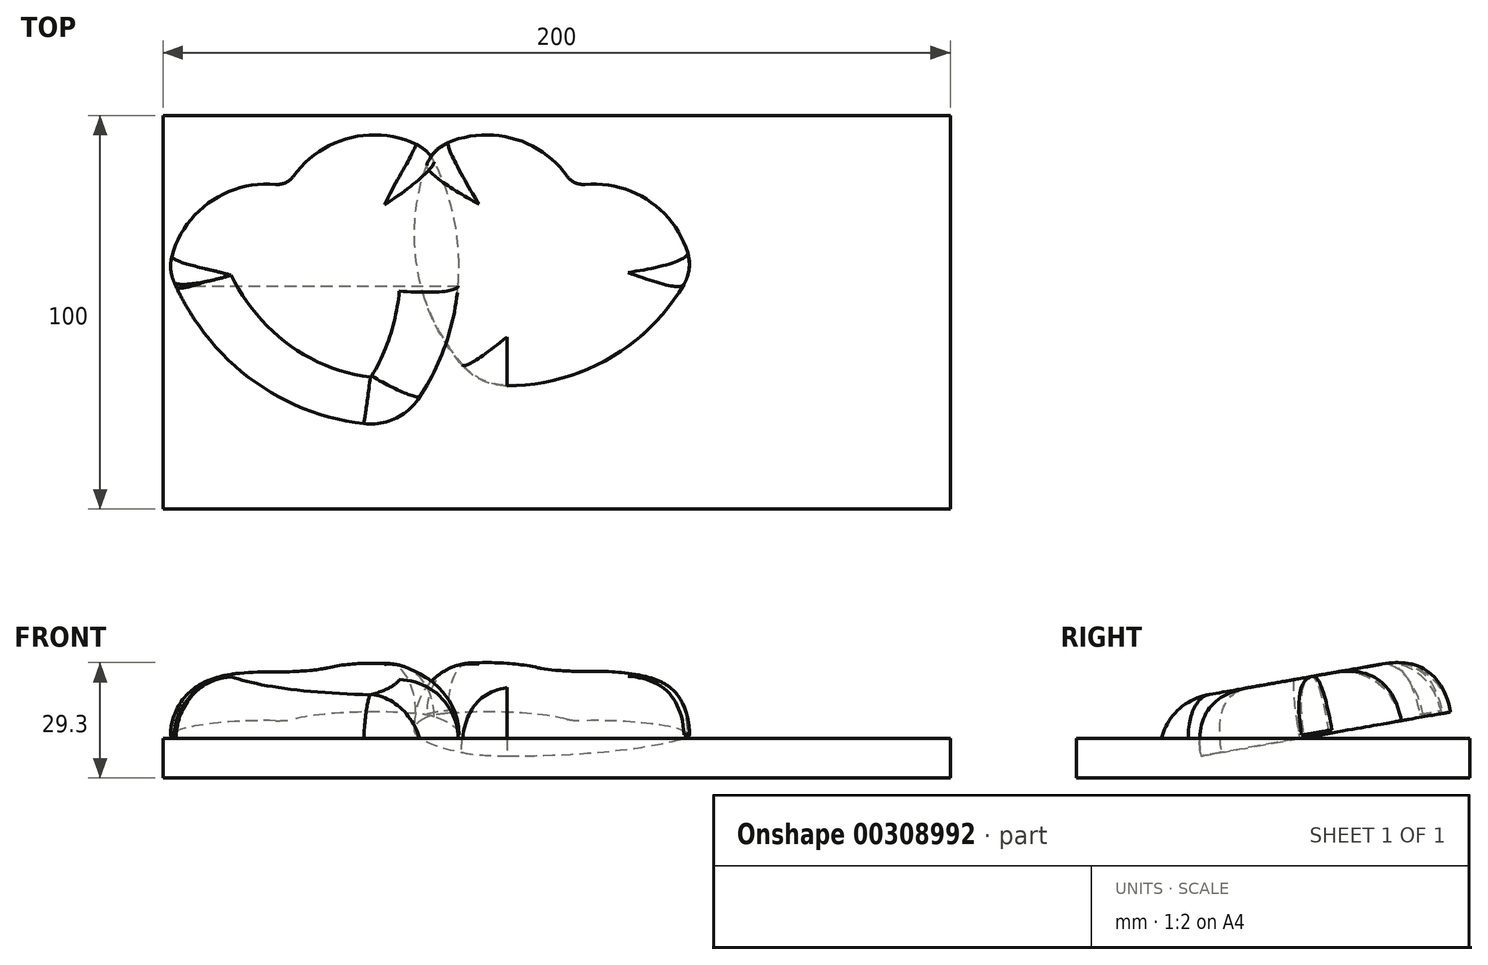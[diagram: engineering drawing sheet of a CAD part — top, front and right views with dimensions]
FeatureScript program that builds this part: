
annotation { "Feature Type Name" : "Feature", "Feature Type Description" : "" }
export const myFeature = defineFeature(function(context is Context, id is Id, definition is map)
    precondition{}
    {
        {
            var Q0;
            Q0=qCreatedBy(makeId("Top.planeOp"),FACE);
            var sketch = newSketch(context, id + "F0", { "sketchPlane" : qUnion([Q0])});
            skLineSegment(sketch, "E0.bottom", {"start": v(0, 0) * mm, "end": v(200, 0) * mm});
            skLineSegment(sketch, "E0.top", {"start": v(0, 100) * mm, "end": v(200, 100) * mm});
            skLineSegment(sketch, "E0.left", {"start": v(0, 0) * mm, "end": v(0, 100) * mm});
            skLineSegment(sketch, "E0.right", {"start": v(200, 0) * mm, "end": v(200, 100) * mm});
            skSolve(sketch);
        }
        {
            var Q0;
            Q0=makeQuery(id+"F0.imprint","IMPRINT",FACE,{"disambiguationData":[TD([[makeQuery(id+"F0.imprint","IMPRINT",EDGE,{"derivedFrom":sQuery(id+"F0.wireOp",EDGE,"E0.bottom")}),1.0]])]});
            extrude(context, id + "F1", {"entities" : qUnion([Q0]), "depth" : 10 * mm});
        }
        {
            var Q0;
            Q0=qCreatedBy(makeId("Top.planeOp"),FACE);
            cPlane(context, id + "F2", {"entities" : qUnion([Q0]), "cplaneType" : CPlaneType.OFFSET, "offset" : 10 * mm, "width" : 150 * mm, "height" : 150 * mm});
        }
        {
            var Q0;
            Q0=qCreatedBy(id+"F2.planeOp",FACE);
            var Q1;
            Q1=makeQuery(id+"F1.opExtrude","CAP_EDGE",EDGE,{"disambiguationData":[OSD([sQuery(id+"F0.wireOp",EDGE,"E0.bottom")])],"isStart":true});
            cPlane(context, id + "F3", {"entities" : qUnion([Q0, Q1]), "cplaneType" : CPlaneType.LINE_ANGLE, "offset" : 25 * mm, "angle" : 170 * degree, "oppositeDirection" : true, "width" : 150 * mm, "height" : 150 * mm});
        }
        {
            var Q0;
            Q0=qCreatedBy(id+"F3.planeOp",FACE);
            var sketch = newSketch(context, id + "F4", { "sketchPlane" : qUnion([Q0])});
            skArc(sketch, "E1", {"start": v(28.58, 83.78) * mm, "mid": v(12.06, 79.35) * mm, "end": v(2.25, 65.33) * mm});
            skArc(sketch, "E2", {"start": v(64.18, 94.2) * mm, "mid": v(47.14, 95.7) * mm, "end": v(33.12, 85.9) * mm});
            skArc(sketch, "E3", {"start": v(65.18, 29.74) * mm, "mid": v(75.06, 59.17) * mm, "end": v(68.9, 89.6) * mm});
            skArc(sketch, "E4", {"start": v(2.75, 58.75) * mm, "mid": v(22.1, 34.48) * mm, "end": v(51, 23.12) * mm});
            skArc(sketch, "E5", {"start": v(102.66, 85.9) * mm, "mid": v(89.03, 95.6) * mm, "end": v(72.33, 94.54) * mm});
            skArc(sketch, "E6", {"start": v(133.3, 66.1) * mm, "mid": v(123.38, 79.58) * mm, "end": v(107.19, 83.78) * mm});
            skArc(sketch, "E7", {"start": v(66.88, 88.77) * mm, "mid": v(64.5, 61.95) * mm, "end": v(75.79, 37.5) * mm});
            skArc(sketch, "E8", {"start": v(87.39, 32.1) * mm, "mid": v(113.38, 39.15) * mm, "end": v(132.4, 58.22) * mm});
            skLineSegment(sketch, "E9", {"start": v(26.4, 58.88) * mm, "end": v(53.6, 71.56) * mm, "construction": true});
            skLineSegment(sketch, "E10", {"start": v(31.55, 83.34) * mm, "end": v(40, 65.22) * mm, "construction": true});
            skLineSegment(sketch, "E11", {"start": v(82.18, 71.56) * mm, "end": v(109.37, 58.88) * mm, "construction": true});
            skLineSegment(sketch, "E12", {"start": v(104.23, 83.34) * mm, "end": v(95.77, 65.22) * mm, "construction": true});
            skPoint(sketch, "E13.visualSharp", {"position": v(1.56, 61.67) * mm});
            skArc(sketch, "E13.filletArc", {"start": v(2.25, 65.33) * mm, "mid": v(1.94, 62) * mm, "end": v(2.75, 58.75) * mm});
            skPoint(sketch, "E14.visualSharp", {"position": v(67.42, 92.38) * mm});
            skArc(sketch, "E14.filletArc", {"start": v(68.9, 89.6) * mm, "mid": v(66.93, 92.3) * mm, "end": v(64.18, 94.2) * mm});
            skPoint(sketch, "E15.visualSharp", {"position": v(68.35, 92.38) * mm});
            skArc(sketch, "E15.filletArc", {"start": v(72.33, 94.54) * mm, "mid": v(69, 92.22) * mm, "end": v(66.88, 88.77) * mm});
            skPoint(sketch, "E16.visualSharp", {"position": v(134.21, 61.67) * mm});
            skArc(sketch, "E16.filletArc", {"start": v(132.4, 58.22) * mm, "mid": v(133.66, 62.07) * mm, "end": v(133.3, 66.1) * mm});
            skPoint(sketch, "E17.visualSharp", {"position": v(104.23, 83.34) * mm});
            skArc(sketch, "E17.filletArc", {"start": v(102.66, 85.9) * mm, "mid": v(104.64, 84.23) * mm, "end": v(107.19, 83.78) * mm});
            skPoint(sketch, "E18.visualSharp", {"position": v(31.55, 83.34) * mm});
            skArc(sketch, "E18.filletArc", {"start": v(28.58, 83.78) * mm, "mid": v(31.13, 84.23) * mm, "end": v(33.12, 85.9) * mm});
            skPoint(sketch, "E19.visualSharp", {"position": v(59.79, 22.78) * mm});
            skArc(sketch, "E19.filletArc", {"start": v(51, 23.12) * mm, "mid": v(59.02, 24.43) * mm, "end": v(65.18, 29.74) * mm});
            skPoint(sketch, "E20.visualSharp", {"position": v(80.52, 32.51) * mm});
            skArc(sketch, "E20.filletArc", {"start": v(75.79, 37.5) * mm, "mid": v(80.98, 33.5) * mm, "end": v(87.39, 32.1) * mm});
            skLineSegment(sketch, "E21", {"start": v(11.91, 62.75) * mm, "end": v(35.93, 73.95) * mm, "construction": true});
            skLineSegment(sketch, "E22", {"start": v(59.95, 85.15) * mm, "end": v(35.93, 73.95) * mm, "construction": true});
            skLineSegment(sketch, "E23", {"start": v(76.27, 85.34) * mm, "end": v(100, 74.28) * mm, "construction": true});
            skPoint(sketch, "E23.endSnap0", {"position": v(100, 74.28) * mm});
            skLineSegment(sketch, "E24", {"start": v(100, 74.28) * mm, "end": v(123.73, 63.22) * mm, "construction": true});
            skSolve(sketch);
        }
        {
            var Q0;
            Q0=makeQuery(id+"F4.imprint","IMPRINT",FACE,{"disambiguationData":[TD([[makeQuery(id+"F4.imprint","IMPRINT",EDGE,{"derivedFrom":sQuery(id+"F4.wireOp",EDGE,"E1")}),1.0]])]});
            var Q1;
            {var subQ0=sQuery(id+"F4.wireOp",EDGE,"E14.filletArc");var subQ1=sQuery(id+"F4.wireOp",EDGE,"E3");var subQ2=makeQuery(id+"F4.imprint","INTERSECT",VERTEX,{"derivedFrom":[subQ1,subQ0]});Q1=makeQuery(id+"F4.imprint","IMPRINT",FACE,{"disambiguationData":[TD([[makeQuery(id+"F4.imprint","IMPRINT",EDGE,{"disambiguationData":[TD([[subQ2,1.0]])],"derivedFrom":subQ1}),1.0]])]});}
            extrude(context, id + "F5", {"entities" : qUnion([Q0, Q1]), "operationType" : NewBodyOperationType.ADD, "depth" : 15 * mm});
        }
        {
            var Q0;
            Q0=makeQuery(id+"F5.opExtrude","CAP_EDGE",EDGE,{"disambiguationData":[OSD([sQuery(id+"F4.wireOp",EDGE,"E4")])],"isStart":false});
            fillet(context, id + "F6", {"entities" : qUnion([Q0]), "radius" : 15 * mm, "tangentPropagation" : true, "allowEdgeOverflow" : false});
        }
        {
            var Q0;
            {var subQ0=sQuery(id+"F4.wireOp",EDGE,"E14.filletArc");var subQ1=sQuery(id+"F4.wireOp",EDGE,"E3");var subQ2=makeQuery(id+"F4.imprint","INTERSECT",VERTEX,{"derivedFrom":[subQ1,subQ0]});Q0=makeQuery(id+"F4.imprint","IMPRINT",FACE,{"disambiguationData":[TD([[makeQuery(id+"F4.imprint","IMPRINT",EDGE,{"disambiguationData":[TD([[subQ2,1.0]])],"derivedFrom":subQ1}),1.0]])]});}
            var Q1;
            {var subQ0=sQuery(id+"F4.wireOp",EDGE,"E5");Q1=makeQuery(id+"F4.imprint","IMPRINT",FACE,{"disambiguationData":[TD([[makeQuery(id+"F4.imprint","IMPRINT",EDGE,{"derivedFrom":subQ0}),1.0]])]});}
            extrude(context, id + "F7", {"entities" : qUnion([Q0, Q1]), "depth" : 15 * mm, "hasDraft" : true, "draftAngle" : 3 * degree, "draftPullDirection" : true});
        }
        {
            var Q0;
            Q0=makeQuery(id+"F7.opExtrude","CAP_EDGE",EDGE,{"disambiguationData":[OSD([sQuery(id+"F4.wireOp",EDGE,"E8")])],"isStart":false});
            fillet(context, id + "F8", {"entities" : qUnion([Q0]), "radius" : 15 * mm, "tangentPropagation" : true, "rho" : 0.5, "crossSection" : FilletCrossSection.CONIC, "allowEdgeOverflow" : false});
        }
    });
